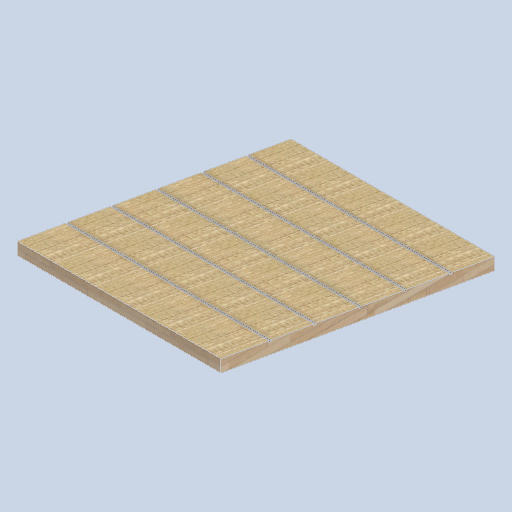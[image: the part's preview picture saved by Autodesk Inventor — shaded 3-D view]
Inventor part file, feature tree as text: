
AUTODESK INVENTOR PART (.ipt)
format: ipt  version: 2024.2 (Build 282272000, 272)  size: 259,072 bytes
history: native  units: in
note: dims shown in document units (in); Inventor stores cm internally (conversion verified against a paired STEP export)
features: sketch x5, other x3, plane x3
ambient origin geometry x8: Origin, YZ Plane, XZ Plane, XY Plane, X Axis, Y Axis, Z Axis, Center Point
bodies: Solid1 (feature_tree)
feature tree (11):
  other  "eave_panel_02.ipt"
  other  "Solid1::eave_panel_02.ipt"
  other  "TaggingFeature1"
  sketch  "Sketch1"  dims[d0=0.3937in]
  sketch  "Sketch2"
  sketch  "Sketch3"
  sketch  "Sketch4"
  sketch  "Sketch5"
  plane  "Work Plane1"
  plane  "Work Plane2"
  plane  "Work Plane3"
